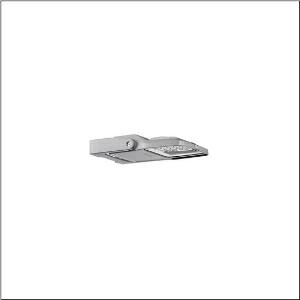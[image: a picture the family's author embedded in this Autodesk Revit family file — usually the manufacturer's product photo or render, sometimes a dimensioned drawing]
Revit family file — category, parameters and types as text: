
# Revit family: floodlight_fl_21_iq_micro___pl43_5xa7761a2a2a_4945
name_source: partatom
category: Lighting Fixtures
units: mm (PartAtom-declared; Revit-internal decimal feet)

## family parameters
Cut with Voids When Loaded = No
Host = Face
Light Source = No
Part Type = Normal
Room Calculation Point = No
Round Connector Dimension = Use Diameter
Shared = No

## types (1)
- --- (1 x LED, 3040 lm, 23.1 W, 3000K)
    Apparent Load = 23 VA
    CIE Flux Codes = 29 80 99 100 100
    Color Rendering = 70
    Color Temperature = 3000K
    Default Elevation = 1800 mm
    Description = Floodlight FL 21 iQ micro, floodlight, primary light control with lens, of PMMA, primary optical cover: protective disc, of toughened safety glass, transparent, light distribution: PL43, light emission: direct distribution, installation type: surface-mounted, LED, High Power LED, rated luminous flux: 3.040lm, luminous efficacy: 132lm/W, light colour: 730, colour temperature: 3000K, control: optimised constant luminous flux control (CLO 2.0), Desk-Remote (wireless, voltage-free reading and setting of iQ features in the workshop via application-optimized NFC function/RFID function), Light-Fading, Smart-Wire, Night-Set, Lumen-Switch, Temp-Guard, Auto-Match, with terminal, 6-pole, mains connection: 220..240V, AC, 50/60Hz, start of lifetime: 23W, end of service life: 24W, reduction: 11W, luminaire housing, of diecast aluminium, powder-coated, Siteco® metallic grey (DB 702S), corrosivity category C5 mid according to DIN EN ISO 12944, sealing non-destructively replaceable, design bracket, of diecast aluminium, powder-coated, Siteco® metallic grey (DB 702S), protection rating (complete): IP66, insulation class (complete): insulation class II (safety insulation), certification: CE, ENEC, VDE, protection symbol: D, impact resistance: IK07, permissible operating ambient temperature: -40..+40°C, permissible operating ambient temperature for outdoor applications: -40..+50°C, standard: DIN EN 12944, LABS conformity tested according to VDMA 24364:2018-05, packaging unit: 1 piece

Light Distribution: PL43
    Height = 65 mm
    Lamp = 1 x LED
    Lamp Light Flux = 3040 lm
    Lamp Power = 23.1 W
    Lamp count = 1
    Length = 312 mm
    Luminous efficacy = 132 lm/W
    Manufacturer = Siteco
    ModVariant = No
    Model = 5XA7761A2A2A
    Mounting Place = Wall
    Mounting Type = Surface mounted
    Number of Poles = 1
    OnlyDefault = Yes
    Power Factor = 1
    Product Name = Floodlight FL 21 iQ micro | PL43
    Product group = floodlight | wall mounted
    ProductGroupID = 2001
    Protection Class = Protection class II
    Protection Degree = IP 66
    RLX_Detail_Level = 1
    RLX_Emergency_Light_Flux = 0 lm
    RLX_Emergency_Type = 0
    RLX_Emergency_Type_DB = No
    RlxData = <blob elided: 97861 chars, md5=d54d3ec4>
    Socket = socket
    Standby Power = 0 W
    System Light Flux = 3040 lm
    System Power = 23 W
    Type Comments = factory setting: luminous flux: 100 % | dim-lin: 254 | 455 mA
    Type Image = l_1006878.jpg
    URL = http://relux.com
    VarID = @adj_128027
    Voltage = 0 V
    Weight = 0.00 kg
    Width = 230 mm

## geometry (parser evidence)
native form markers: Blend x4, Sweep x14
no freeform markers — native parametric forms only
